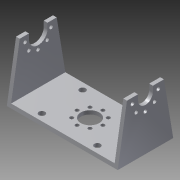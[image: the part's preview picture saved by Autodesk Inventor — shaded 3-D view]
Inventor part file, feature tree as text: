
AUTODESK INVENTOR PART (.ipt)
format: ipt  version: 2013 (Build 170138000, 138)  size: 200,192 bytes
history: native  units: mm
features: sketch x8, extrude x4, hole x4, pattern_circular x2, other x1
ambient origin geometry x8: Origin, YZ Plane, XZ Plane, XY Plane, X Axis, Y Axis, Z Axis, Center Point
feature tree (19):
  other  "ソリッド1"
  extrude  "押し出し1"  Depth=60.0mm
  extrude  "押し出し2"  Depth=30.0mm
  extrude  "押し出し3"  Depth=28.0mm
  extrude  "押し出し4"  Depth=56.0mm
  hole  "穴2"  [1 undecoded]
  hole  "穴3"  [1 undecoded]
  pattern_circular  "円形状パターン2"  Count=3  [1 undecoded]
  hole  "穴4"  [1 undecoded]
  pattern_circular  "円形状パターン3"  [2 undecoded]
  hole  "穴5"  [1 undecoded]
  sketch  "スケッチ1"
  sketch  "スケッチ2"
  sketch  "スケッチ3"
  sketch  "スケッチ4"
  sketch  "スケッチ7"
  sketch  "スケッチ8"
  sketch  "スケッチ9"
  sketch  "スケッチ10"
note: 7 required parameter values undecoded (feature->parameter linkage not recoverable at this tier; creation-order binding heuristic only, values carry confidence <= 0.55)
